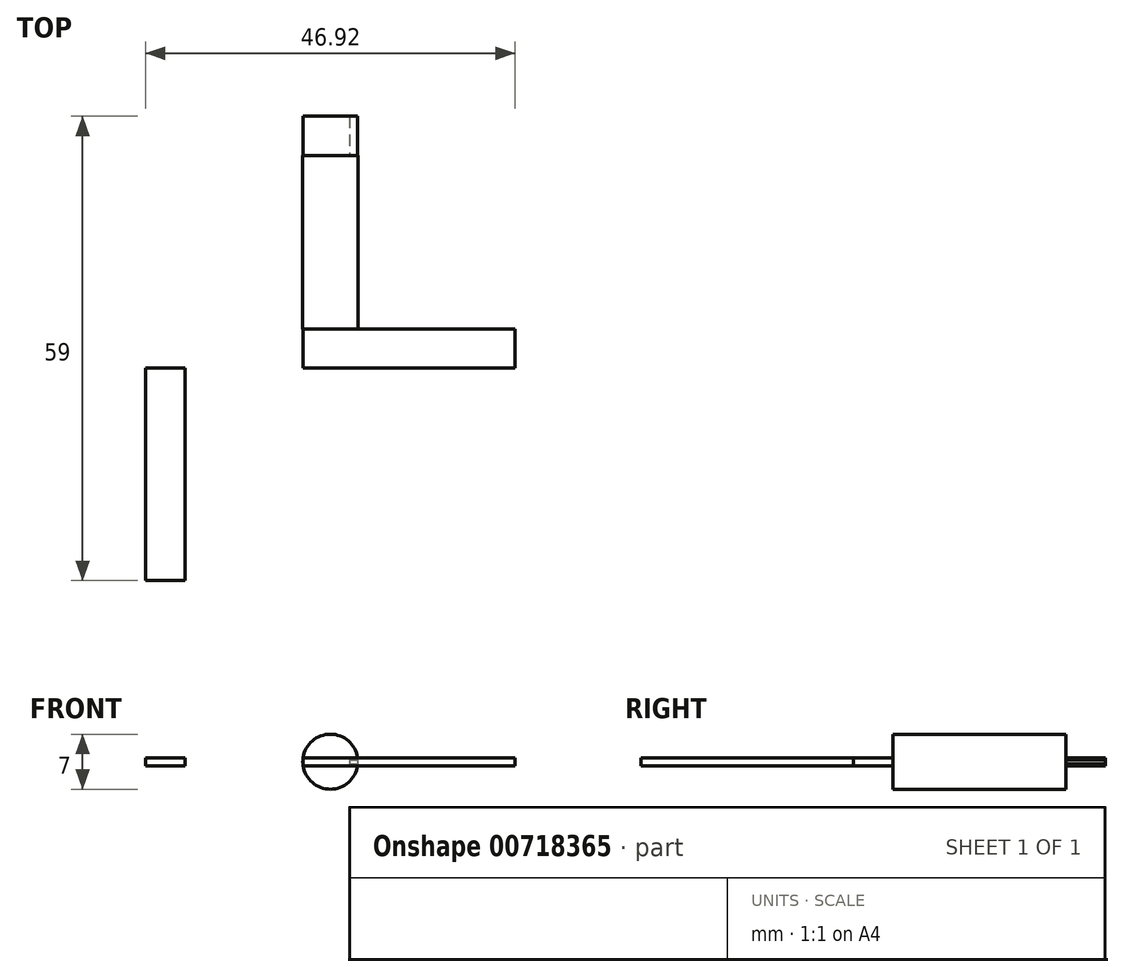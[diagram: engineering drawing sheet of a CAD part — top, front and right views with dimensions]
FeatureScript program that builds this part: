
annotation { "Feature Type Name" : "Feature", "Feature Type Description" : "" }
export const myFeature = defineFeature(function(context is Context, id is Id, definition is map)
    precondition{}
    {
        {
            var Q0;
            Q0=qCreatedBy(makeId("Front.planeOp"),FACE);
            var sketch = newSketch(context, id + "F0", { "sketchPlane" : qUnion([Q0])});
            skCircle(sketch, "E0", {"center": v(0, 0) * mm, "radius": 3.5 * mm});
            skLineSegment(sketch, "E1.bottom", {"start": v(3.5, -3.5) * mm, "end": v(-3.5, -3.5) * mm});
            skLineSegment(sketch, "E1.top", {"start": v(3.5, 3.5) * mm, "end": v(-3.5, 3.5) * mm});
            skLineSegment(sketch, "E1.left", {"start": v(3.5, -3.5) * mm, "end": v(3.5, 3.5) * mm});
            skLineSegment(sketch, "E1.right", {"start": v(-3.5, -3.5) * mm, "end": v(-3.5, 3.5) * mm});
            skSolve(sketch);
        }
        {
            var Q0;
            Q0=makeQuery(id+"F0.imprint","IMPRINT",FACE,{"disambiguationData":[TD([[makeQuery(id+"F0.imprint","IMPRINT",EDGE,{"derivedFrom":sQuery(id+"F0.wireOp",EDGE,"E0")}),1.0]])]});
            var Q1;
            {var subQ0=sQuery(id+"F0.wireOp",EDGE,"E1.top");var subQ1=sQuery(id+"F0.wireOp",EDGE,"E0");var subQ2=makeQuery(id+"F0.imprint","INTERSECT",VERTEX,{"derivedFrom":[subQ1,subQ0]});Q1=makeQuery(id+"F0.imprint","IMPRINT",FACE,{"disambiguationData":[TD([[makeQuery(id+"F0.imprint","IMPRINT",EDGE,{"disambiguationData":[TD([[subQ2,-1.0]])],"derivedFrom":subQ1}),-1.0]])]});}
            var Q2;
            {var subQ0=sQuery(id+"F0.wireOp",EDGE,"E1.right");var subQ1=sQuery(id+"F0.wireOp",EDGE,"E0");var subQ2=makeQuery(id+"F0.imprint","INTERSECT",VERTEX,{"derivedFrom":[subQ1,subQ0]});Q2=makeQuery(id+"F0.imprint","IMPRINT",FACE,{"disambiguationData":[TD([[makeQuery(id+"F0.imprint","IMPRINT",EDGE,{"disambiguationData":[TD([[subQ2,-1.0]])],"derivedFrom":subQ1}),-1.0]])]});}
            var Q3;
            {var subQ0=sQuery(id+"F0.wireOp",EDGE,"E1.left");var subQ1=sQuery(id+"F0.wireOp",EDGE,"E0");var subQ2=makeQuery(id+"F0.imprint","INTERSECT",VERTEX,{"derivedFrom":[subQ1,subQ0]});Q3=makeQuery(id+"F0.imprint","IMPRINT",FACE,{"disambiguationData":[TD([[makeQuery(id+"F0.imprint","IMPRINT",EDGE,{"disambiguationData":[TD([[subQ2,1.0]])],"derivedFrom":subQ1}),-1.0]])]});}
            var Q4;
            {var subQ0=sQuery(id+"F0.wireOp",EDGE,"E1.top");var subQ1=sQuery(id+"F0.wireOp",EDGE,"E0");var subQ2=makeQuery(id+"F0.imprint","INTERSECT",VERTEX,{"derivedFrom":[subQ1,subQ0]});Q4=makeQuery(id+"F0.imprint","IMPRINT",FACE,{"disambiguationData":[TD([[makeQuery(id+"F0.imprint","IMPRINT",EDGE,{"disambiguationData":[TD([[subQ2,1.0]])],"derivedFrom":subQ1}),-1.0]])]});}
            extrude(context, id + "F1", {"entities" : qUnion([Q0, Q1, Q2, Q3, Q4]), "depth" : 22 * mm, "offsetDistance" : 25 * mm});
        }
        {
            var Q0;
            Q0=makeQuery(id+"F1.opExtrude","CAP_FACE",FACE,{"disambiguationData":[OSD([sQuery(id+"F0.wireOp",EDGE,"E1.bottom"),sQuery(id+"F0.wireOp",EDGE,"E1.top"),sQuery(id+"F0.wireOp",EDGE,"E1.left"),sQuery(id+"F0.wireOp",EDGE,"E1.right")])],"isStart":false});
            var sketch = newSketch(context, id + "F2", { "sketchPlane" : qUnion([Q0])});
            skCircle(sketch, "E2", {"center": v(0, 0) * mm, "radius": 3.5 * mm});
            skLineSegment(sketch, "E3", {"start": v(0, 0.5) * mm, "end": v(-3.46, 0.5) * mm});
            skLineSegment(sketch, "E4.bottom", {"start": v(-3.46, 0.5) * mm, "end": v(3.46, 0.5) * mm});
            skLineSegment(sketch, "E4.top", {"start": v(-3.46, -0.5) * mm, "end": v(3.46, -0.5) * mm});
            skLineSegment(sketch, "E4.left", {"start": v(-3.46, 0.5) * mm, "end": v(-3.46, -0.5) * mm});
            skLineSegment(sketch, "E4.right", {"start": v(3.46, 0.5) * mm, "end": v(3.46, -0.5) * mm});
            skSolve(sketch);
        }
        {
            var Q0;
            Q0=makeQuery(id+"F2.imprint","IMPRINT",FACE,{"disambiguationData":[TD([[makeQuery(id+"F2.imprint","IMPRINT",EDGE,{"derivedFrom":sQuery(id+"F2.wireOp",EDGE,"E4.top")}),1.0]])]});
            extrude(context, id + "F3", {"entities" : qUnion([Q0]), "operationType" : NewBodyOperationType.ADD, "depth" : 5 * mm, "offsetDistance" : 25 * mm});
        }
        {
            var Q0;
            Q0=makeQuery(id+"F1.opExtrude","CAP_FACE",FACE,{"disambiguationData":[OSD([sQuery(id+"F0.wireOp",EDGE,"E1.bottom"),sQuery(id+"F0.wireOp",EDGE,"E1.top"),sQuery(id+"F0.wireOp",EDGE,"E1.left"),sQuery(id+"F0.wireOp",EDGE,"E1.right")])],"isStart":true});
            var sketch = newSketch(context, id + "F4", { "sketchPlane" : qUnion([Q0])});
            skCircle(sketch, "E5", {"center": v(0, 0) * mm, "radius": 3.5 * mm});
            skLineSegment(sketch, "E6", {"start": v(0, -0.5) * mm, "end": v(3.46, -0.5) * mm});
            skLineSegment(sketch, "E7", {"start": v(0, 0.5) * mm, "end": v(-3.46, 0.5) * mm});
            skLineSegment(sketch, "E8.bottom", {"start": v(-3.46, 0.5) * mm, "end": v(3.46, 0.5) * mm});
            skLineSegment(sketch, "E8.top", {"start": v(-3.46, -0.5) * mm, "end": v(3.46, -0.5) * mm});
            skLineSegment(sketch, "E8.left", {"start": v(-3.46, 0.5) * mm, "end": v(-3.46, -0.5) * mm});
            skLineSegment(sketch, "E8.right", {"start": v(3.46, 0.5) * mm, "end": v(3.46, -0.5) * mm});
            skSolve(sketch);
        }
        {
            var Q0;
            {var subQ4=sQuery(id+"F4.wireOp",EDGE,"E8.left");Q0=makeQuery(id+"F4.imprint","IMPRINT",FACE,{"disambiguationData":[TD([[makeQuery(id+"F4.imprint","IMPRINT",EDGE,{"derivedFrom":subQ4}),1.0]])]});}
            extrude(context, id + "F5", {"entities" : qUnion([Q0]), "operationType" : NewBodyOperationType.ADD, "depth" : 5 * mm, "offsetDistance" : 25 * mm});
        }
        {
            var Q0;
            Q0=makeQuery(id+"F1.opExtrude","CAP_FACE",FACE,{"disambiguationData":[OSD([sQuery(id+"F0.wireOp",EDGE,"E1.bottom"),sQuery(id+"F0.wireOp",EDGE,"E1.top"),sQuery(id+"F0.wireOp",EDGE,"E1.left"),sQuery(id+"F0.wireOp",EDGE,"E1.right")])],"isStart":true});
            var sketch = newSketch(context, id + "F6", { "sketchPlane" : qUnion([Q0])});
            skArc(sketch, "E9", {"start": v(3.5, 0) * mm, "mid": v(2.47, 2.47) * mm, "end": v(0, 3.5) * mm});
            skArc(sketch, "E10", {"start": v(0, -3.5) * mm, "mid": v(2.47, -2.47) * mm, "end": v(3.5, 0) * mm});
            skArc(sketch, "E11", {"start": v(0, 3.5) * mm, "mid": v(-2.47, 2.47) * mm, "end": v(-3.5, 0) * mm});
            skArc(sketch, "E12", {"start": v(-3.5, 0) * mm, "mid": v(-2.47, -2.47) * mm, "end": v(0, -3.5) * mm});
            skSolve(sketch);
        }
        {
            var Q0;
            {var subQ2=makeQuery(id+"F1.opExtrude","CAP_EDGE",EDGE,{"disambiguationData":[OSD([sQuery(id+"F0.wireOp",EDGE,"E1.top")])],"isStart":true});var subQ4=makeQuery(id+"F1.opExtrude","CAP_EDGE",EDGE,{"disambiguationData":[OSD([sQuery(id+"F0.wireOp",EDGE,"E1.left")])],"isStart":true});var subQ5=makeQuery(id+"F6.imprint","INTERSECT",VERTEX,{"derivedFrom":[subQ2,subQ4]});Q0=makeQuery(id+"F6.imprint","IMPRINT",FACE,{"disambiguationData":[TD([[makeQuery(id+"F6.imprint","IMPRINT",EDGE,{"disambiguationData":[TD([[subQ5,-1.0]])],"derivedFrom":subQ2}),-1.0]])]});}
            var Q1;
            {var subQ2=makeQuery(id+"F1.opExtrude","CAP_EDGE",EDGE,{"disambiguationData":[OSD([sQuery(id+"F0.wireOp",EDGE,"E1.right")])],"isStart":true});var subQ4=makeQuery(id+"F1.opExtrude","CAP_EDGE",EDGE,{"disambiguationData":[OSD([sQuery(id+"F0.wireOp",EDGE,"E1.top")])],"isStart":true});var subQ5=makeQuery(id+"F6.imprint","INTERSECT",VERTEX,{"derivedFrom":[subQ4,subQ2]});Q1=makeQuery(id+"F6.imprint","IMPRINT",FACE,{"disambiguationData":[TD([[makeQuery(id+"F6.imprint","IMPRINT",EDGE,{"disambiguationData":[TD([[subQ5,1.0]])],"derivedFrom":subQ4}),-1.0]])]});}
            var Q2;
            {var subQ2=makeQuery(id+"F1.opExtrude","CAP_EDGE",EDGE,{"disambiguationData":[OSD([sQuery(id+"F0.wireOp",EDGE,"E1.left")])],"isStart":true});var subQ4=makeQuery(id+"F1.opExtrude","CAP_EDGE",EDGE,{"disambiguationData":[OSD([sQuery(id+"F0.wireOp",EDGE,"E1.bottom")])],"isStart":true});var subQ5=makeQuery(id+"F6.imprint","INTERSECT",VERTEX,{"derivedFrom":[subQ4,subQ2]});Q2=makeQuery(id+"F6.imprint","IMPRINT",FACE,{"disambiguationData":[TD([[makeQuery(id+"F6.imprint","IMPRINT",EDGE,{"disambiguationData":[TD([[subQ5,-1.0]])],"derivedFrom":subQ4}),1.0]])]});}
            var Q3;
            {var subQ2=makeQuery(id+"F1.opExtrude","CAP_EDGE",EDGE,{"disambiguationData":[OSD([sQuery(id+"F0.wireOp",EDGE,"E1.bottom")])],"isStart":true});var subQ4=makeQuery(id+"F1.opExtrude","CAP_EDGE",EDGE,{"disambiguationData":[OSD([sQuery(id+"F0.wireOp",EDGE,"E1.right")])],"isStart":true});var subQ6=makeQuery(id+"F6.imprint","INTERSECT",VERTEX,{"derivedFrom":[subQ2,subQ4]});Q3=makeQuery(id+"F6.imprint","IMPRINT",FACE,{"disambiguationData":[TD([[makeQuery(id+"F6.imprint","IMPRINT",EDGE,{"disambiguationData":[TD([[subQ6,1.0]])],"derivedFrom":subQ2}),1.0]])]});}
            extrude(context, id + "F7", {"entities" : qUnion([Q0, Q1, Q2, Q3]), "operationType" : NewBodyOperationType.REMOVE, "oppositeDirection" : true, "depth" : 25 * mm, "offsetDistance" : 25 * mm});
        }
        {
            var Q0;
            Q0=makeQuery(id+"F3.opExtrude","SWEPT_FACE",FACE,{"disambiguationData":[OSD([sQuery(id+"F2.wireOp",EDGE,"E4.right")])]});
            extrude(context, id + "F8", {"entities" : qUnion([Q0]), "operationType" : NewBodyOperationType.ADD, "depth" : 20 * mm, "offsetDistance" : 25 * mm});
        }
        {
            var Q0;
            {var subQ0=sQuery(id+"F2.wireOp",EDGE,"E4.right");Q0=makeQuery(id+"F8.opExtrude","SWEPT_FACE",FACE,{"disambiguationData":[OSD([subQ0]),TDD([makeQuery(id+"F3.opExtrude","CAP_EDGE",EDGE,{"disambiguationData":[OSD([subQ0])],"isStart":true})])]});}
            var sketch = newSketch(context, id + "F9", { "sketchPlane" : qUnion([Q0])});
            skLineSegment(sketch, "E13.bottom", {"start": v(-23.46, 0.5) * mm, "end": v(-18.46, 0.5) * mm});
            skLineSegment(sketch, "E13.top", {"start": v(-23.46, -0.5) * mm, "end": v(-18.46, -0.5) * mm});
            skLineSegment(sketch, "E13.left", {"start": v(-23.46, 0.5) * mm, "end": v(-23.46, -0.5) * mm});
            skLineSegment(sketch, "E13.right", {"start": v(-18.46, 0.5) * mm, "end": v(-18.46, -0.5) * mm});
            skSolve(sketch);
        }
        {
            var Q0;
            Q0=makeQuery(id+"F9.imprint","IMPRINT",FACE,{"disambiguationData":[TD([[makeQuery(id+"F9.imprint","IMPRINT",EDGE,{"derivedFrom":sQuery(id+"F9.wireOp",EDGE,"E13.bottom")}),-1.0]])]});
            extrude(context, id + "F10", {"entities" : qUnion([Q0]), "operationType" : NewBodyOperationType.ADD, "depth" : 27 * mm, "offsetDistance" : 25 * mm});
        }
        {
            var Q0;
            Q0=makeQuery(id+"F10.opExtrude","SWEPT_FACE",FACE,{"disambiguationData":[OSD([sQuery(id+"F9.wireOp",EDGE,"E13.right")])]});
            var sketch = newSketch(context, id + "F11", { "sketchPlane" : qUnion([Q0])});
            skLineSegment(sketch, "E14", {"start": v(-5, 0.5) * mm, "end": v(-5, 0.25) * mm});
            skLineSegment(sketch, "E15", {"start": v(-5, -0.5) * mm, "end": v(-5, -0.25) * mm});
            skLineSegment(sketch, "E16.bottom", {"start": v(-5, 0.25) * mm, "end": v(0, 0.25) * mm});
            skLineSegment(sketch, "E16.top", {"start": v(-5, -0.25) * mm, "end": v(0, -0.25) * mm});
            skLineSegment(sketch, "E16.left", {"start": v(-5, 0.25) * mm, "end": v(-5, -0.25) * mm});
            skLineSegment(sketch, "E16.right", {"start": v(0, 0.25) * mm, "end": v(0, -0.25) * mm});
            skSolve(sketch);
        }
        {
            var Q0;
            Q0=makeQuery(id+"F11.imprint","IMPRINT",FACE,{"disambiguationData":[TD([[makeQuery(id+"F11.imprint","IMPRINT",EDGE,{"derivedFrom":sQuery(id+"F11.wireOp",EDGE,"E16.bottom")}),-1.0]])]});
            extrude(context, id + "F12", {"entities" : qUnion([Q0]), "operationType" : NewBodyOperationType.REMOVE, "oppositeDirection" : true, "depth" : 1 * mm, "offsetDistance" : 25 * mm});
        }
        {
            var Q0;
            Q0=makeQuery(id+"F5.opExtrude","SWEPT_FACE",FACE,{"disambiguationData":[OSD([sQuery(id+"F4.wireOp",EDGE,"E8.left")])]});
            var sketch = newSketch(context, id + "F13", { "sketchPlane" : qUnion([Q0])});
            skLineSegment(sketch, "E17", {"start": v(5, 0.5) * mm, "end": v(5, 0.25) * mm});
            skLineSegment(sketch, "E18", {"start": v(5, -0.5) * mm, "end": v(5, -0.25) * mm});
            skLineSegment(sketch, "E19.bottom", {"start": v(5, 0.25) * mm, "end": v(0, 0.25) * mm});
            skLineSegment(sketch, "E19.top", {"start": v(5, -0.25) * mm, "end": v(0, -0.25) * mm});
            skLineSegment(sketch, "E19.left", {"start": v(5, 0.25) * mm, "end": v(5, -0.25) * mm});
            skLineSegment(sketch, "E19.right", {"start": v(0, 0.25) * mm, "end": v(0, -0.25) * mm});
            skSolve(sketch);
        }
        {
            var Q0;
            Q0=makeQuery(id+"F13.imprint","IMPRINT",FACE,{"disambiguationData":[TD([[makeQuery(id+"F13.imprint","IMPRINT",EDGE,{"derivedFrom":sQuery(id+"F13.wireOp",EDGE,"E19.bottom")}),1.0]])]});
            extrude(context, id + "F14", {"entities" : qUnion([Q0]), "operationType" : NewBodyOperationType.REMOVE, "oppositeDirection" : true, "depth" : 1 * mm, "offsetDistance" : 25 * mm});
        }
    });
